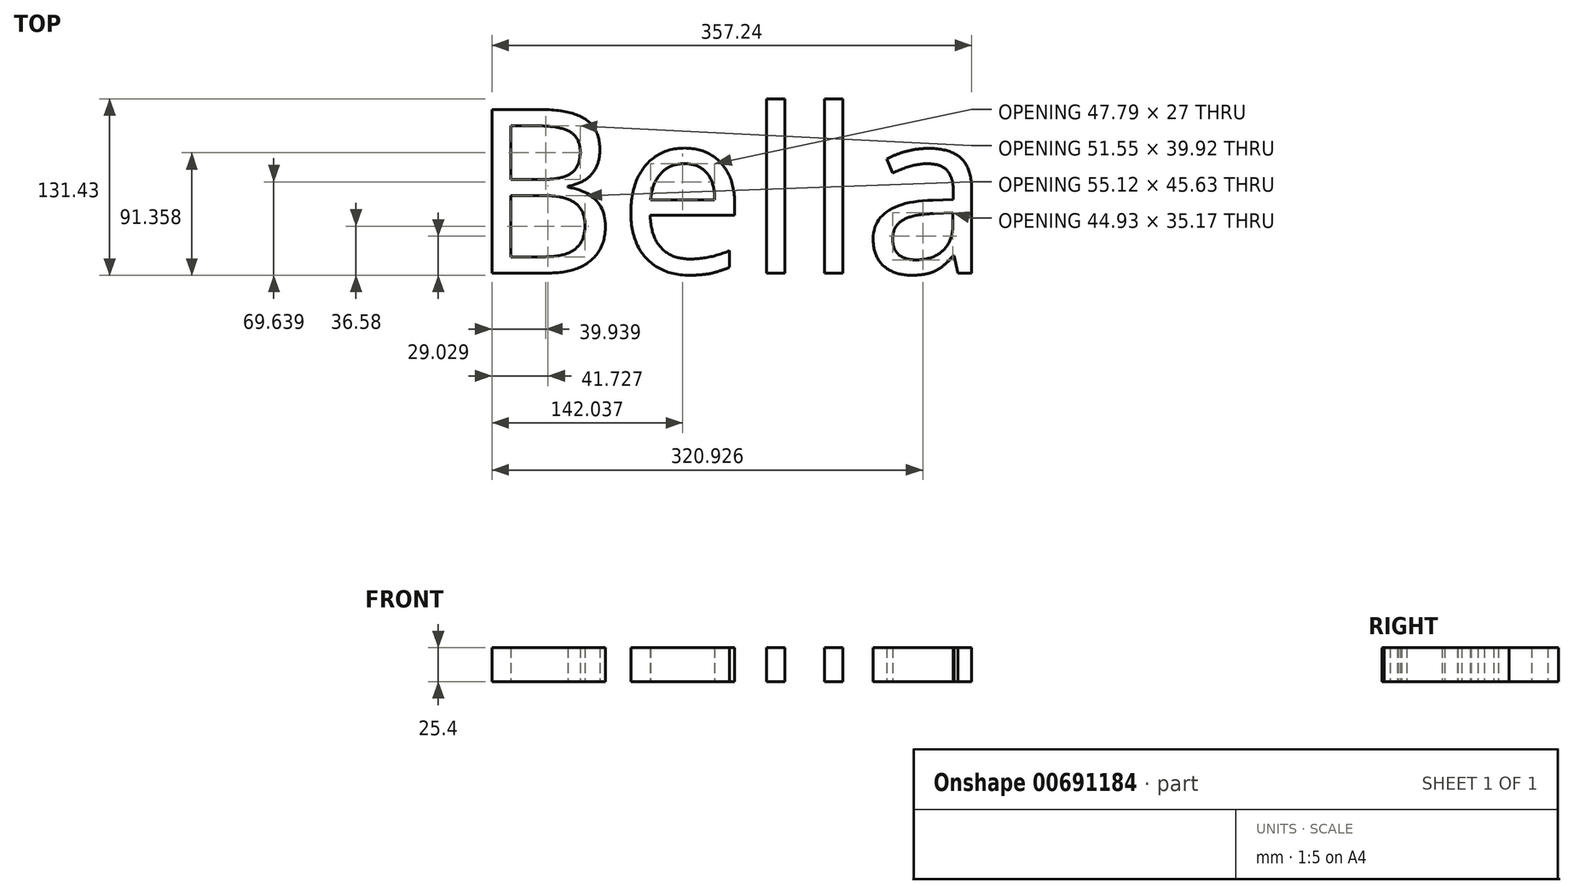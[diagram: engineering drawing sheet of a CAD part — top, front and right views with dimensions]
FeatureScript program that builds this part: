
annotation { "Feature Type Name" : "Feature", "Feature Type Description" : "" }
export const myFeature = defineFeature(function(context is Context, id is Id, definition is map)
    precondition{}
    {
        {
            var Q0;
            Q0=qCreatedBy(makeId("Top.planeOp"),FACE);
            var sketch = newSketch(context, id + "F0", { "sketchPlane" : qUnion([Q0])});
            skText(sketch, "E0", { "text": "Bella\n", "fontName": "OpenSans-Regular.ttf"});
            const initialGuessF0  = {"E0": [-0.14994, -0.05826, 1, 0, 0.12295]};
            skSetInitialGuess(sketch, initialGuessF0);
            skSolve(sketch);
        }
        {
            var Q0;
            Q0=qSketchRegion(id+"F0",true);
            extrude(context, id + "F1", {"entities" : qUnion([Q0]), "depth" : 25.4 * mm});
        }
    });
